# Revit family: Domotics-DomesticRanges-GEWISS-CHORUS_POWER-SOCKET-OUTLET_FAST_WIRING_GER
name_source: partatom
category: Apparecchi elettrici
revit_build: Autodesk Revit 2016 (Build: 20161004_0715(x64)
units: mm (PartAtom-declared; Revit-internal decimal feet)

## family parameters
Condiviso = Sì
Host = Superficie
Mantenere orientamento annotazione = Sì
Punto di calcolo locali = Sì
Quota connettore circolare = Usa diametro
Taglio con vuoti quando caricato = Sì
Tipo di parte = Normale

## types (4) — shared parameters
Breaking capacity: = 1.25 In (100 position changes)
Carico apparente = 0 VA
Catalogue = DOMOTICS
Catalogue Range = CHORUS - DOMESTIC RANGE
Category = Dual amperage socket-outlet
Characteristics = With safety shields
Description. = Dual amperage socket-outlet
Description: = 2P+E - 16A
Electrocod = 0131
For plug pins = Ã˜ 4.8 mm
Glow Wire Test = 850°C
IDF = 0c5e28e7-5aa1-4d2c-ab25-04cfa7fbd197
IDT = 1fcd8efb-8fc7-42a6-9204-03fcfbf25279
Immagine tipo = GW14241F.jpg
Insulation resistance = > 5 MOhm
N. poli = 1
No. Chorus modules = 2
No. Chorus modules: = 2
Produttore = GEWISS S.p.A.
Prolonged operation (no.of position changes) = 10.000 at In 250 V ac cosÃ˜=0,8
Prospetto di default = 1219 mm
Resistance at test voltage = 2000 V at 50 Hz for 1 minute
SEO = Socket outlet
Standard = German
Standard: = German
Standard; = IEC 60884-1; DIN VDE 0620-1
TXT ELETTRICO = 16
Technical sheet = https://www.gewiss.com
Terminal grip on cable traction = > 50 N
Terminal tightening capacity flexible cables (mm2) = min. 0,75 - max. 2x4
Terminal tightening capacity rigid cables (mm2) = min. 0,5 - max. 2x2,5
Thermo-pressure with ball = 125
Tipo_ = Chorus Prese Ger_GENERICO : GW14241F Presa 2M 2P+T 16A morsetti cabl. rapido standard Tedesco titanio
Type = Quick wiring
URL = https://www.gewiss.com
Version file RFA = 19.0
Volt = 230 V
Voltage = 250 V ac
Voltage: = 250 V ac
Wiring terminals = Quick, with spring

## per-type parameters (varying)
| type | Colour | Descrizione | EAN code | Modello |
| GW10241F - Socket outlet 2M 2P+E 16A de quick wiring white | White | S. OUT. 2M 2P+E 16A DE QUICK WIRING WH | 8011564425019 | GW10241F |
| GW10251F - Socket outlet 2M 2P+E 16A de quick wiring red | Red | S. OUT. 2M 2P+E 16A DE QUICK WIRING RED | 8011564425026 | GW10251F |
| GW12241F - Socket outlet 2M 2P+E 16A germ. o.q.wiring black | Black | 2M 2P+E 16A GERM.SOCKET O.Q.WIRING BLACK | 8011564425033 | GW12241F |
| GW14241F - Socket outlet 2M 2P+E 16A germ. o.q.wiring titanium | Titanium | 2M 2P+E 16A GERM.SOCKET O.Q.WIRING TIT. | 8011564425040 | GW14241F |

note: source unit labels omitted for Thermo-pressure with ball — the stored unit's dimension contradicts the parameter name (converter mislabeling)

## geometry (parser evidence)
native form markers: Sweep x2
no freeform markers — native parametric forms only
